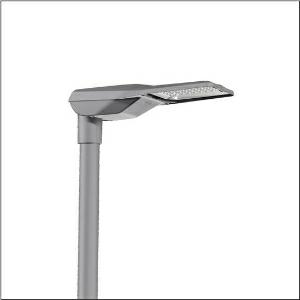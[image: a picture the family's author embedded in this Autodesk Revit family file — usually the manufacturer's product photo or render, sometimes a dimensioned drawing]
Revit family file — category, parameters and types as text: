
# Revit family: streetlight_sl_21_iq_mini___p0_5a_5xe2v31g08gb_39a9
name_source: partatom
category: Lighting Fixtures
units: mm (PartAtom-declared; Revit-internal decimal feet)

## family parameters
Cut with Voids When Loaded = No
Host = Face
Light Source = No
Part Type = Normal
Room Calculation Point = No
Round Connector Dimension = Use Diameter
Shared = No

## types (1)
- --- (1 x LED, 5580 lm, 37.1 W, 3000K)
    Apparent Load = 37 VA
    CIE Flux Codes = 37 73 96 100 100
    Color Rendering = 70
    Color Temperature = 3000K
    Default Elevation = 1800 mm
    Description = Streetlight SL 21 iQ mini, mast luminaire, primary light control with lens, of PMMA, primary optical cover: cover, of toughened safety glass, transparent, light distribution: P0.5a, light emission: direct distribution, primary light characteristic: asymmetric, installation type: post-top, side-entry, LED, High Power LED, rated luminous flux: 5.580lm, luminous efficacy: 150lm/W, light colour: 730, colour temperature: 3000K, control gear: iQ Street-Remote, control: pre-setting: linear dimming characteristic, Street-Remote, Auto-Match, Temp-Guard, Lumen-Switch, Night-Set, Smart-Wire, Light-Fading, Desk-Remote (wireless, voltage-free reading and setting of iQ features in the workshop via application-optimized NFC function/RFID function), optimised constant luminous flux control (CLO 2.0), mains connection: 220..240V, AC, 50/60Hz, start of lifetime: 37W, end of service life: 39W, reduction: 18W, luminaire housing, of diecast aluminium, powder-coated, SITECO metallic grey (DB 702S), corrosivity category C5 high according to DIN EN ISO 12944, please order mast flange separately, inclination adjustable: 0°, 5°, 10°, 15°, sealing non-destructively replaceable, multi-level sealing system, length: 628mm, width: 235mm, height: 110mm, mast flange for spigot size: 42mm (side-entry): 5XC10008XM4, 60/48mm (side-entry/post-top): 5XC10108XM2, 76/60mm (side-entry/post-top): 5XC10108XM1, mounting height: 4..8m, protection rating (complete): IP66, insulation class (complete): insulation class II (safety insulation), certification: CE, ENEC, ENEC+, VDE, impact resistance: IK10, permissible operating ambient temperature for outdoor applications: -40..+50°C, standard-compliant lighting for roads and squares, packaging unit: 1 piece

Light Distribution: P0.5a
    Height = 110 mm
    Lamp = 1 x LED
    Lamp Light Flux = 5580 lm
    Lamp Power = 37.1 W
    Lamp count = 1
    Length = 625 mm
    Luminous efficacy = 150 lm/W
    Manufacturer = Siteco
    ModVariant = No
    Model = 5XE2V31G08GB
    Number of Poles = 1
    OnlyDefault = Yes
    Power Factor = 1
    Product Name = Streetlight SL 21 iQ mini | P0.5a
    Product group = mast luminaire | pylon top
    ProductGroupID = 6100
    Protection Class = Protection class II
    Protection Degree = IP 66
    RLX_Detail_Level = 1
    RLX_Emergency_Light_Flux = 0 lm
    RLX_Emergency_Type = 0
    RLX_Emergency_Type_DB = No
    RlxData = <blob elided: 92069 chars, md5=195ea5fb>
    Socket = socket
    Standby Power = 0 W
    System Light Flux = 5580 lm
    System Power = 37 W
    Type Comments = factory setting: luminous flux: 100 % | dim-lin: 254 | 385 mA
    Type Image = l_1003519.jpg
    URL = http://relux.com
    VarID = @adj_077731
    Voltage = 0 V
    Weight = 0.00 kg
    Width = 234 mm

## geometry (parser evidence)
native form markers: Blend x4, Sweep x12
no freeform markers — native parametric forms only
